# Revit family: БП220 исп3_RV17_LOD400 (05.11.23)
name_source: partatom
category: Электрооборудование
revit_build: Autodesk Revit 2017 (Build: 20170118_1100(x64)
units: mm (PartAtom-declared; Revit-internal decimal feet)

## family parameters
Всегда вертикально = Нет
Конфигурация панели = Два столбца, слева направо
На основе рабочей плоскости = Да
Общий = Нет
При загрузке вырезать с полостями = Нет
Размер круглого соединителя = Использовать диаметр
Тип детали = Щит
Точка расчета площади = Нет

## types (1)
- БП220 исп3
    ADSK_URL страницы изделия = https://stilsoft.ru
    ADSK_Единица измерения = шт.
    ADSK_Завод-изготовитель = ООО «Основа Безопасности»
    ADSK_Количество = 1
    ADSK_Марка = СТВФ.426471.015-01
    ADSK_Масса = 2.2
    ADSK_Наименование = Блок питания 220В/12В БП220
    ADSK_Размер_Высота = 56 мм
    ADSK_Размер_Глубина = 166 мм
    ADSK_Размер_Длина = 299 мм
    d_короба = 0 мм
    Время непрерывной работы, ч = круглосуточно
    Выходной ток, А = 29 А
    Диапазон рабочих температур, °С = от –40 до +50
    Интерфейс управления = RS-485
    Максимальный потребляемый ток, не более, А = 4 А
    Напряжение = 12
    Номинальный потребляемый ток, не более, А = 2 А
    Отметка по умолчанию = 1219 мм
